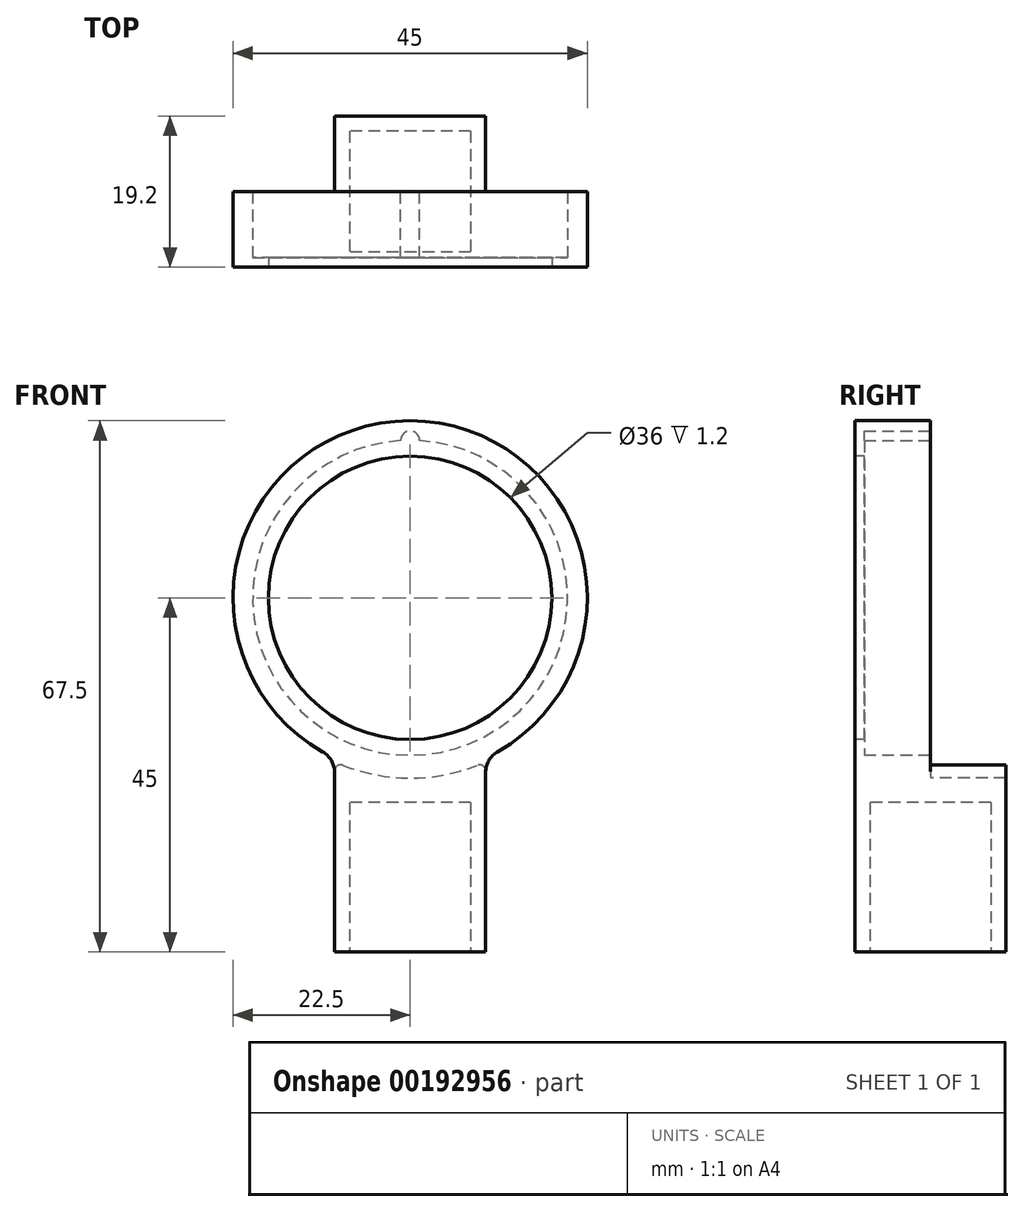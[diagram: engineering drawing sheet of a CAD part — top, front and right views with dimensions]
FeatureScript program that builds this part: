
annotation { "Feature Type Name" : "Feature", "Feature Type Description" : "" }
export const myFeature = defineFeature(function(context is Context, id is Id, definition is map)
    precondition{}
    {
        {
            var Q0;
            Q0=qCreatedBy(makeId("Top.planeOp"),FACE);
            var sketch = newSketch(context, id + "F0", { "sketchPlane" : qUnion([Q0])});
            skLineSegment(sketch, "E0.bottom", {"start": v(9.6, -9.6) * mm, "end": v(-9.6, -9.6) * mm});
            skLineSegment(sketch, "E0.top", {"start": v(9.6, 9.6) * mm, "end": v(-9.6, 9.6) * mm});
            skLineSegment(sketch, "E0.left", {"start": v(9.6, -9.6) * mm, "end": v(9.6, 9.6) * mm});
            skLineSegment(sketch, "E0.right", {"start": v(-9.6, -9.6) * mm, "end": v(-9.6, 9.6) * mm});
            skPoint(sketch, "E0.middle", {"position": v(0, 0) * mm});
            skSolve(sketch);
        }
        {
            var Q0;
            Q0 = qSketchRegion(id + "F0", true);
            extrude(context, id + "F1", {"entities" : qUnion([Q0]), "depth" : 25 * mm});
        }
        {
            var Q0;
            Q0=makeQuery(id+"F1.opExtrude","SWEPT_FACE",FACE,{"disambiguationData":[OSD([sQuery(id+"F0.wireOp",EDGE,"E0.bottom")])]});
            var sketch = newSketch(context, id + "F2", { "sketchPlane" : qUnion([Q0])});
            skCircle(sketch, "E1", {"center": v(0, 45) * mm, "radius": 22.5 * mm});
            skPoint(sketch, "E1.centerSnap0", {"position": v(0, 25) * mm});
            skSolve(sketch);
        }
        {
            var Q0;
            Q0 = qSketchRegion(id + "F2", true);
            extrude(context, id + "F3", {"entities" : qUnion([Q0]), "operationType" : NewBodyOperationType.ADD, "oppositeDirection" : true, "depth" : (19.2 / 2) * mm});
        }
        {
            var Q0;
            Q0=makeQuery(id+"F3.boolean.opBoolean","MERGE",FACE,{"derivedFrom":[makeQuery(id+"F1.opExtrude","SWEPT_FACE",FACE,{"disambiguationData":[OSD([sQuery(id+"F0.wireOp",EDGE,"E0.bottom")])]}),makeQuery(id+"F3.opExtrude","CAP_FACE",FACE,{"disambiguationData":[OSD([sQuery(id+"F2.wireOp",EDGE,"E1")])],"isStart":true})]});
            var sketch = newSketch(context, id + "F4", { "sketchPlane" : qUnion([Q0])});
            skCircle(sketch, "E2", {"center": v(0, 45) * mm, "radius": 20 * mm});
            skSolve(sketch);
        }
        {
            var Q0;
            Q0 = qSketchRegion(id + "F4", true);
            extrude(context, id + "F5", {"entities" : qUnion([Q0]), "operationType" : NewBodyOperationType.REMOVE, "oppositeDirection" : true, "depth" : 25 * mm});
        }
        {
            var Q0;
            Q0=makeQuery(id+"F3.opExtrude","CAP_FACE",FACE,{"disambiguationData":[OSD([sQuery(id+"F2.wireOp",EDGE,"E1")])],"isStart":false});
            var sketch = newSketch(context, id + "F6", { "sketchPlane" : qUnion([Q0])});
            skCircle(sketch, "E3", {"center": v(0, 45) * mm, "radius": 22.9 * mm});
            skSolve(sketch);
        }
        {
            var Q0;
            Q0 = qSketchRegion(id + "F6", true);
            extrude(context, id + "F7", {"entities" : qUnion([Q0]), "operationType" : NewBodyOperationType.REMOVE, "depth" : 25 * mm});
        }
        {
            var Q0;
            Q0=makeQuery(id+"F3.boolean.opBoolean","INTERSECT",EDGE,{"derivedFrom":[makeQuery(id+"F1.opExtrude","SWEPT_FACE",FACE,{"disambiguationData":[OSD([sQuery(id+"F0.wireOp",EDGE,"E0.left")])]}),makeQuery(id+"F3.opExtrude","SWEPT_FACE",FACE,{"disambiguationData":[OSD([sQuery(id+"F2.wireOp",EDGE,"E1")])]})]});
            var Q1;
            Q1=makeQuery(id+"F3.boolean.opBoolean","INTERSECT",EDGE,{"derivedFrom":[makeQuery(id+"F1.opExtrude","SWEPT_FACE",FACE,{"disambiguationData":[OSD([sQuery(id+"F0.wireOp",EDGE,"E0.right")])]}),makeQuery(id+"F3.opExtrude","SWEPT_FACE",FACE,{"disambiguationData":[OSD([sQuery(id+"F2.wireOp",EDGE,"E1")])]})]});
            fillet(context, id + "F8", {"entities" : qUnion([Q0, Q1]), "radius" : 3 * mm, "tangentPropagation" : true, "allowEdgeOverflow" : false});
        }
        {
            var Q0;
            Q0=makeQuery(id+"F8.opFillet","BLEND_EDGE",EDGE,{"blendedFrom":[makeQuery(id+"F3.boolean.opBoolean","INTERSECT",EDGE,{"derivedFrom":[makeQuery(id+"F1.opExtrude","SWEPT_FACE",FACE,{"disambiguationData":[OSD([sQuery(id+"F0.wireOp",EDGE,"E0.right")])]}),makeQuery(id+"F3.opExtrude","SWEPT_FACE",FACE,{"disambiguationData":[OSD([sQuery(id+"F2.wireOp",EDGE,"E1")])]})]}),makeQuery(id+"F7.boolean.opBoolean","COPY",FACE,{"derivedFrom":makeQuery(id+"F7.opExtrude","SWEPT_FACE",FACE,{"disambiguationData":[OSD([sQuery(id+"F6.wireOp",EDGE,"E3")])]})})],"blendedInto":[makeQuery(id+"F7.boolean.opBoolean","COPY",FACE,{"derivedFrom":makeQuery(id+"F7.opExtrude","SWEPT_FACE",FACE,{"disambiguationData":[OSD([sQuery(id+"F6.wireOp",EDGE,"E3")])]})})]});
            var Q1;
            Q1=makeQuery(id+"F8.opFillet","BLEND_EDGE",EDGE,{"blendedFrom":[makeQuery(id+"F3.boolean.opBoolean","INTERSECT",EDGE,{"derivedFrom":[makeQuery(id+"F1.opExtrude","SWEPT_FACE",FACE,{"disambiguationData":[OSD([sQuery(id+"F0.wireOp",EDGE,"E0.left")])]}),makeQuery(id+"F3.opExtrude","SWEPT_FACE",FACE,{"disambiguationData":[OSD([sQuery(id+"F2.wireOp",EDGE,"E1")])]})]}),makeQuery(id+"F7.boolean.opBoolean","COPY",FACE,{"derivedFrom":makeQuery(id+"F7.opExtrude","SWEPT_FACE",FACE,{"disambiguationData":[OSD([sQuery(id+"F6.wireOp",EDGE,"E3")])]})})],"blendedInto":[makeQuery(id+"F7.boolean.opBoolean","COPY",FACE,{"derivedFrom":makeQuery(id+"F7.opExtrude","SWEPT_FACE",FACE,{"disambiguationData":[OSD([sQuery(id+"F6.wireOp",EDGE,"E3")])]})})]});
            fillet(context, id + "F9", {"entities" : qUnion([Q0, Q1]), "radius" : 0.8 * mm, "tangentPropagation" : true, "allowEdgeOverflow" : false});
        }
        {
            var Q0;
            Q0=makeQuery(id+"F3.boolean.opBoolean","MERGE",FACE,{"derivedFrom":[makeQuery(id+"F1.opExtrude","SWEPT_FACE",FACE,{"disambiguationData":[OSD([sQuery(id+"F0.wireOp",EDGE,"E0.bottom")])]}),makeQuery(id+"F3.opExtrude","CAP_FACE",FACE,{"disambiguationData":[OSD([sQuery(id+"F2.wireOp",EDGE,"E1")])],"isStart":true})]});
            var sketch = newSketch(context, id + "F10", { "sketchPlane" : qUnion([Q0])});
            skCircle(sketch, "E4", {"center": v(0, 45) * mm, "radius": 20.5 * mm});
            skCircle(sketch, "E5", {"center": v(0, 45) * mm, "radius": 18 * mm});
            skSolve(sketch);
        }
        {
            var Q0;
            Q0 = qSketchRegion(id + "F10", true);
            extrude(context, id + "F11", {"entities" : qUnion([Q0]), "operationType" : NewBodyOperationType.ADD, "oppositeDirection" : true, "depth" : 1.2 * mm});
        }
        {
            var Q0;
            Q0=makeQuery(id+"F7.boolean.opBoolean","MERGE",FACE,{"derivedFrom":[makeQuery(id+"F3.opExtrude","CAP_FACE",FACE,{"disambiguationData":[OSD([sQuery(id+"F2.wireOp",EDGE,"E1")])],"isStart":false}),makeQuery(id+"F7.opExtrude","CAP_FACE",FACE,{"disambiguationData":[OSD([sQuery(id+"F6.wireOp",EDGE,"E3")])],"isStart":true})]});
            var sketch = newSketch(context, id + "F12", { "sketchPlane" : qUnion([Q0])});
            skCircle(sketch, "E6", {"center": v(0, 65) * mm, "radius": 1.2 * mm});
            skSolve(sketch);
        }
        {
            var Q0;
            Q0 = qSketchRegion(id + "F12", true);
            var Q1;
            Q1=makeQuery(id+"F11.opExtrude","CAP_FACE",FACE,{"disambiguationData":[OSD([sQuery(id+"F10.wireOp",EDGE,"E4"),sQuery(id+"F10.wireOp",EDGE,"E5")])],"isStart":false});
            extrude(context, id + "F13", {"entities" : qUnion([Q0]), "operationType" : NewBodyOperationType.REMOVE, "endBound" : BoundingType.UP_TO_SURFACE, "oppositeDirection" : true, "endBoundEntityFace" : qUnion([Q1]), "depth" : 25 * mm});
        }
        {
            var Q0;
            Q0=makeQuery(id+"F1.opExtrude","CAP_FACE",FACE,{"disambiguationData":[OSD([sQuery(id+"F0.wireOp",EDGE,"E0.bottom"),sQuery(id+"F0.wireOp",EDGE,"E0.top"),sQuery(id+"F0.wireOp",EDGE,"E0.left"),sQuery(id+"F0.wireOp",EDGE,"E0.right")])],"isStart":true});
            var sketch = newSketch(context, id + "F14", { "sketchPlane" : qUnion([Q0])});
            skLineSegment(sketch, "E7.bottom", {"start": v(7.7, -7.7) * mm, "end": v(-7.7, -7.7) * mm});
            skLineSegment(sketch, "E7.top", {"start": v(7.7, 7.7) * mm, "end": v(-7.7, 7.7) * mm});
            skLineSegment(sketch, "E7.left", {"start": v(7.7, -7.7) * mm, "end": v(7.7, 7.7) * mm});
            skLineSegment(sketch, "E7.right", {"start": v(-7.7, -7.7) * mm, "end": v(-7.7, 7.7) * mm});
            skPoint(sketch, "E7.middle", {"position": v(0, 0) * mm});
            skSolve(sketch);
        }
        {
            var Q0;
            Q0 = qSketchRegion(id + "F14", true);
            extrude(context, id + "F15", {"entities" : qUnion([Q0]), "operationType" : NewBodyOperationType.REMOVE, "oppositeDirection" : true, "depth" : 19 * mm});
        }
    });
